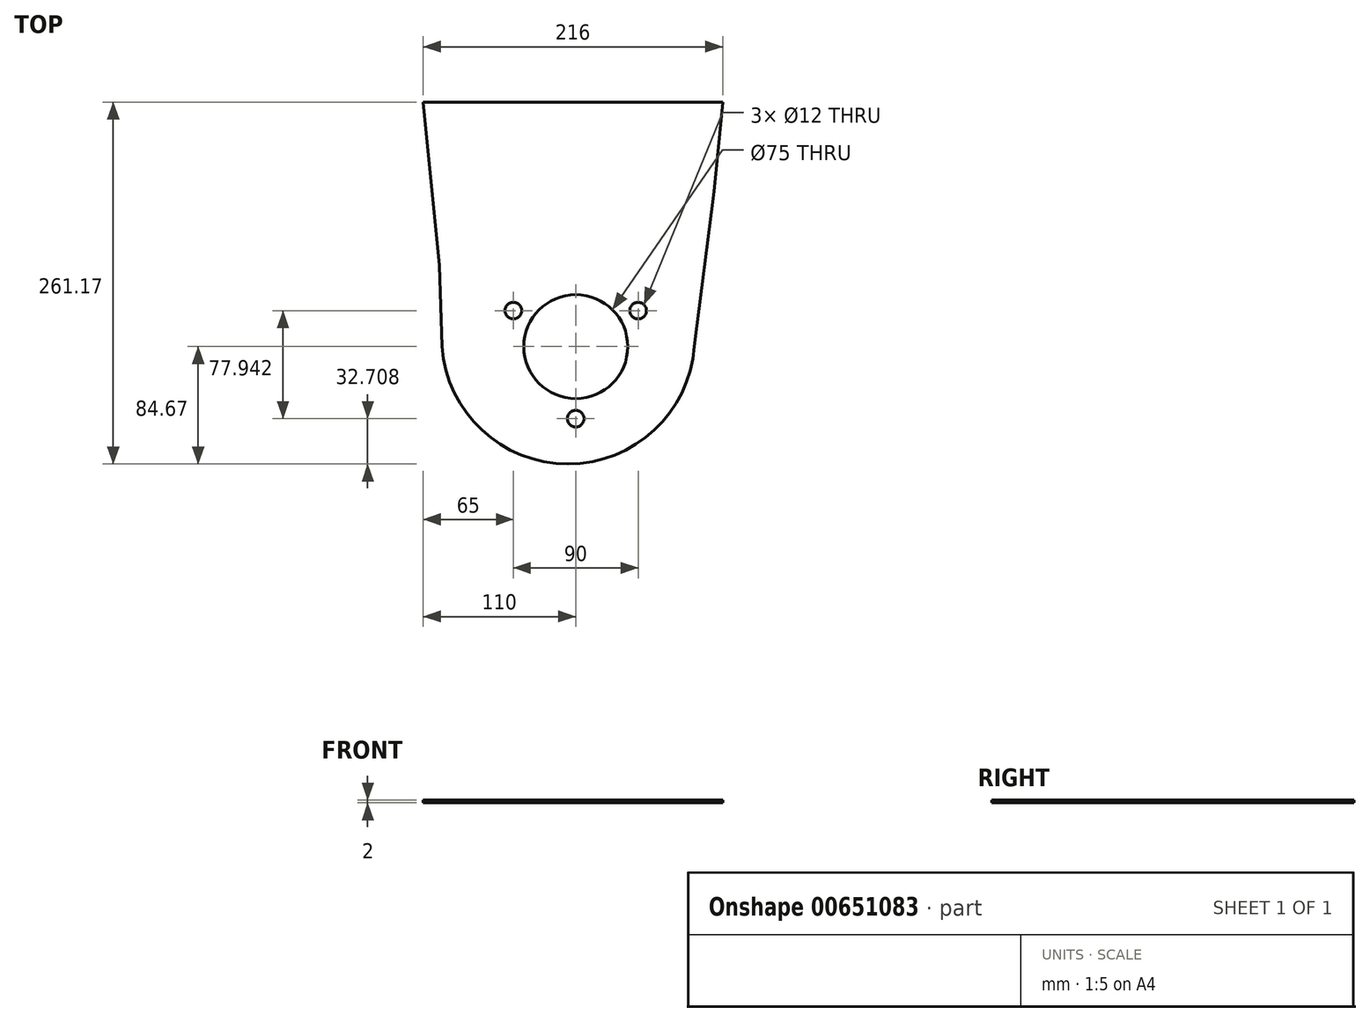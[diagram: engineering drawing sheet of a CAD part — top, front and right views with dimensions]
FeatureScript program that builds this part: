
annotation { "Feature Type Name" : "Feature", "Feature Type Description" : "" }
export const myFeature = defineFeature(function(context is Context, id is Id, definition is map)
    precondition{}
    {
        {
            var Q0;
            Q0=qCreatedBy(makeId("Top.planeOp"),FACE);
            var sketch = newSketch(context, id + "F0", { "sketchPlane" : qUnion([Q0])});
            skCircle(sketch, "E0", {"center": v(0, 0) * mm, "radius": 37.5 * mm});
            skLineSegment(sketch, "E1", {"start": v(37.5, 0) * mm, "end": v(85.5, 0) * mm, "construction": true});
            skLineSegment(sketch, "E2", {"start": v(-37.5, 0) * mm, "end": v(-96.5, 0) * mm, "construction": true});
            skLineSegment(sketch, "E3", {"start": v(0, -37.5) * mm, "end": v(0, -84.5) * mm, "construction": true});
            skArc(sketch, "E4", {"start": v(-96.5, 0) * mm, "mid": v(-5.5, -84.67) * mm, "end": v(85.5, 0) * mm});
            skLineSegment(sketch, "E5", {"start": v(0, 37.5) * mm, "end": v(0, 176.5) * mm, "construction": true});
            skLineSegment(sketch, "E6", {"start": v(106, 176.5) * mm, "end": v(-110, 176.5) * mm});
            skLineSegment(sketch, "E7", {"start": v(-98.32, 58.56) * mm, "end": v(99.83, 112.02) * mm, "construction": true});
            skCircle(sketch, "E8", {"center": v(-45, 25.98) * mm, "radius": 6 * mm});
            skCircle(sketch, "E9", {"center": v(45, 25.98) * mm, "radius": 6 * mm});
            skCircle(sketch, "E10", {"center": v(0, -51.96) * mm, "radius": 6 * mm});
            skCircle(sketch, "E11", {"center": v(0, 0) * mm, "radius": 52 * mm, "construction": true});
            skLineSegment(sketch, "E12", {"start": v(-96.5, 0) * mm, "end": v(-98.32, 58.56) * mm});
            skLineSegment(sketch, "E13", {"start": v(85.5, 0) * mm, "end": v(99.83, 112.02) * mm});
            skLineSegment(sketch, "E14", {"start": v(99.83, 112.02) * mm, "end": v(106, 176.5) * mm});
            skLineSegment(sketch, "E15", {"start": v(-98.32, 58.56) * mm, "end": v(-110, 176.5) * mm});
            skSolve(sketch);
        }
        {
            var Q0;
            Q0=makeQuery(id+"F0.imprint","IMPRINT",FACE,{"disambiguationData":[TD([[makeQuery(id+"F0.imprint","IMPRINT",EDGE,{"derivedFrom":sQuery(id+"F0.wireOp",EDGE,"E0")}),-1.0]])]});
            extrude(context, id + "F1", {"entities" : qUnion([Q0]), "depth" : 2 * mm, "offsetDistance" : 25 * mm});
        }
    });
